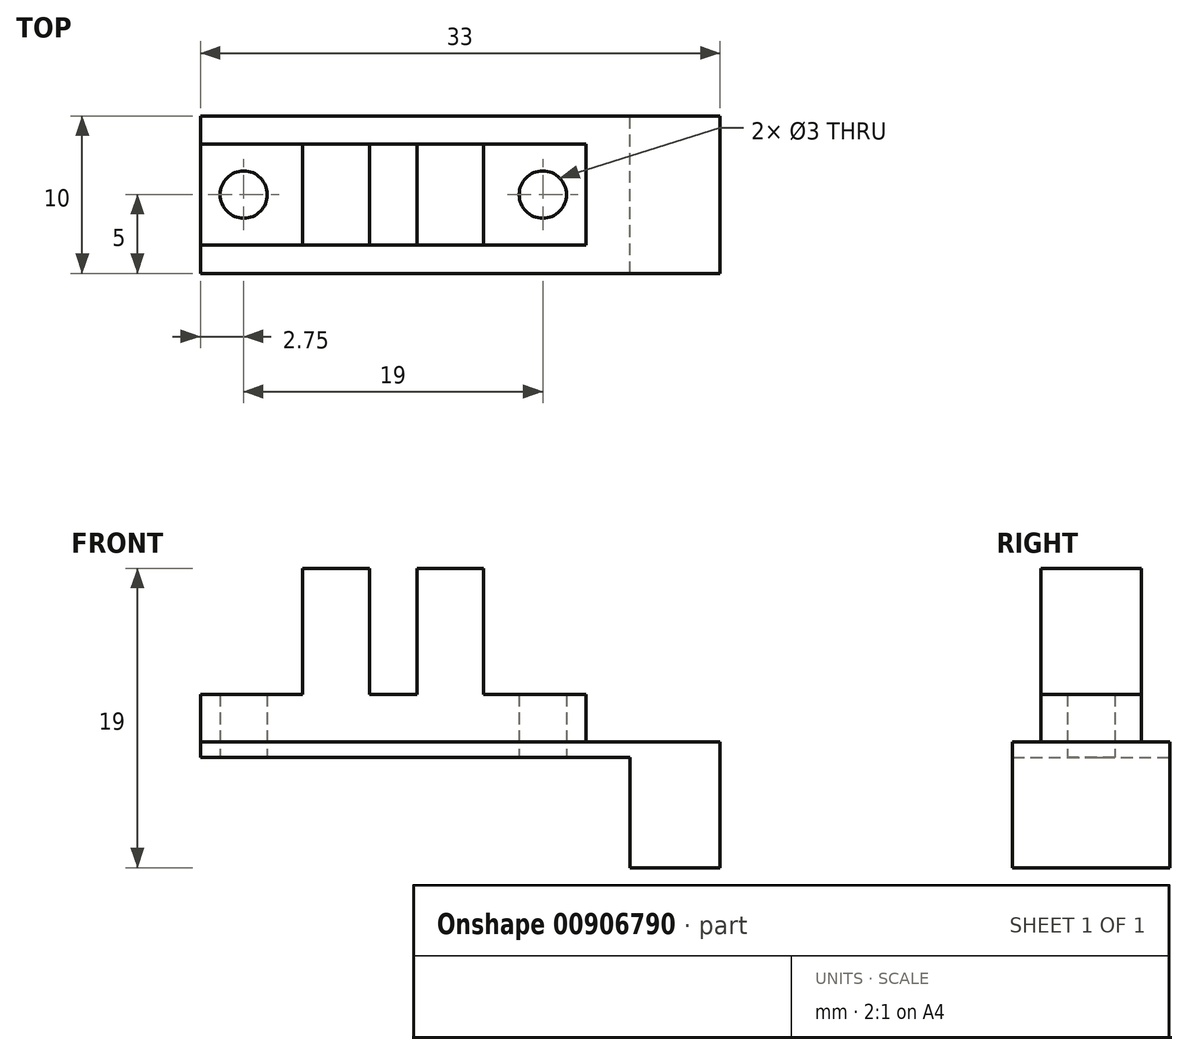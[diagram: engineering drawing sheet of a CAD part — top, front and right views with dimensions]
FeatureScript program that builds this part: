
annotation { "Feature Type Name" : "Feature", "Feature Type Description" : "" }
export const myFeature = defineFeature(function(context is Context, id is Id, definition is map)
    precondition{}
    {
        {
            var Q0;
            Q0=qCreatedBy(makeId("Top.planeOp"),FACE);
            var sketch = newSketch(context, id + "F0", { "sketchPlane" : qUnion([Q0])});
            skCircle(sketch, "E0", {"center": v(-9.5, 0) * mm, "radius": 1.5 * mm});
            skCircle(sketch, "E1", {"center": v(9.5, 0) * mm, "radius": 1.5 * mm});
            skLineSegment(sketch, "E2.bottom", {"start": v(12.25, -5) * mm, "end": v(-12.25, -5) * mm});
            skLineSegment(sketch, "E2.top", {"start": v(12.25, 5) * mm, "end": v(-12.25, 5) * mm});
            skLineSegment(sketch, "E2.left", {"start": v(12.25, -5) * mm, "end": v(12.25, 5) * mm});
            skLineSegment(sketch, "E2.right", {"start": v(-12.25, -5) * mm, "end": v(-12.25, 5) * mm});
            skPoint(sketch, "E2.middle", {"position": v(0, 0) * mm});
            skLineSegment(sketch, "E3", {"start": v(12.25, 5) * mm, "end": v(20.75, 5) * mm});
            skLineSegment(sketch, "E4", {"start": v(20.75, 5) * mm, "end": v(20.75, -5) * mm});
            skLineSegment(sketch, "E5", {"start": v(20.75, -5) * mm, "end": v(12.25, -5) * mm});
            skSolve(sketch);
        }
        {
            var Q0;
            Q0=makeQuery(id+"F0.imprint","IMPRINT",FACE,{"disambiguationData":[TD([[makeQuery(id+"F0.imprint","IMPRINT",EDGE,{"derivedFrom":sQuery(id+"F0.wireOp",EDGE,"E0")}),-1.0]])]});
            var Q1;
            Q1=makeQuery(id+"F0.imprint","IMPRINT",FACE,{"disambiguationData":[TD([[makeQuery(id+"F0.imprint","IMPRINT",EDGE,{"derivedFrom":sQuery(id+"F0.wireOp",EDGE,"E2.left")}),-1.0]])]});
            extrude(context, id + "F1", {"entities" : qUnion([Q0, Q1]), "depth" : 1 * mm, "offsetDistance" : 25 * mm});
        }
        {
            var Q0;
            Q0=makeQuery(id+"F1.opExtrude","CAP_FACE",FACE,{"disambiguationData":[OSD([sQuery(id+"F0.wireOp",EDGE,"E0"),sQuery(id+"F0.wireOp",EDGE,"E1"),sQuery(id+"F0.wireOp",EDGE,"E2.bottom"),sQuery(id+"F0.wireOp",EDGE,"E2.top"),sQuery(id+"F0.wireOp",EDGE,"E2.right"),sQuery(id+"F0.wireOp",EDGE,"E3"),sQuery(id+"F0.wireOp",EDGE,"E4"),sQuery(id+"F0.wireOp",EDGE,"E5")])],"isStart":false});
            var sketch = newSketch(context, id + "F2", { "sketchPlane" : qUnion([Q0])});
            skLineSegment(sketch, "E6.bottom", {"start": v(-12.25, -3.2) * mm, "end": v(12.25, -3.2) * mm});
            skLineSegment(sketch, "E6.top", {"start": v(-12.25, 3.2) * mm, "end": v(12.25, 3.2) * mm});
            skLineSegment(sketch, "E6.left", {"start": v(-12.25, -3.2) * mm, "end": v(-12.25, 3.2) * mm});
            skLineSegment(sketch, "E6.right", {"start": v(12.25, -3.2) * mm, "end": v(12.25, 3.2) * mm});
            skPoint(sketch, "E6.middle", {"position": v(0, 0) * mm});
            skLineSegment(sketch, "E7", {"start": v(-5.75, 3.2) * mm, "end": v(-5.75, -3.2) * mm});
            skLineSegment(sketch, "E8", {"start": v(-1.5, 3.2) * mm, "end": v(-1.5, -3.2) * mm});
            skLineSegment(sketch, "E9", {"start": v(1.5, -3.2) * mm, "end": v(1.5, 3.2) * mm});
            skLineSegment(sketch, "E10", {"start": v(5.75, 3.2) * mm, "end": v(5.75, -3.2) * mm});
            skLineSegment(sketch, "E11", {"start": v(0, 3.2) * mm, "end": v(0, -3.2) * mm, "construction": true});
            skSolve(sketch);
        }
        {
            var Q0;
            {var subQ1=sQuery(id+"F2.wireOp",EDGE,"E6.left");Q0=makeQuery(id+"F2.imprint","IMPRINT",FACE,{"disambiguationData":[TD([[makeQuery(id+"F2.imprint","IMPRINT",EDGE,{"derivedFrom":subQ1}),-1.0]])]});}
            var Q1;
            {var subQ0=sQuery(id+"F2.wireOp",EDGE,"E8");Q1=makeQuery(id+"F2.imprint","IMPRINT",FACE,{"disambiguationData":[TD([[makeQuery(id+"F2.imprint","IMPRINT",EDGE,{"derivedFrom":subQ0}),1.0]])]});}
            var Q2;
            {var subQ1=sQuery(id+"F2.wireOp",EDGE,"E6.right");Q2=makeQuery(id+"F2.imprint","IMPRINT",FACE,{"disambiguationData":[TD([[makeQuery(id+"F2.imprint","IMPRINT",EDGE,{"derivedFrom":subQ1}),1.0]])]});}
            extrude(context, id + "F3", {"entities" : qUnion([Q0, Q1, Q2]), "operationType" : NewBodyOperationType.ADD, "depth" : 3 * mm, "offsetDistance" : 25 * mm});
        }
        {
            var Q0;
            {var subQ0=sQuery(id+"F2.wireOp",EDGE,"E7");Q0=makeQuery(id+"F2.imprint","IMPRINT",FACE,{"disambiguationData":[TD([[makeQuery(id+"F2.imprint","IMPRINT",EDGE,{"derivedFrom":subQ0}),1.0]])]});}
            var Q1;
            {var subQ0=sQuery(id+"F2.wireOp",EDGE,"E9");Q1=makeQuery(id+"F2.imprint","IMPRINT",FACE,{"disambiguationData":[TD([[makeQuery(id+"F2.imprint","IMPRINT",EDGE,{"derivedFrom":subQ0}),-1.0]])]});}
            extrude(context, id + "F4", {"entities" : qUnion([Q0, Q1]), "operationType" : NewBodyOperationType.ADD, "depth" : 11 * mm, "offsetDistance" : 25 * mm});
        }
        {
            var Q0;
            Q0=makeQuery(id+"F1.opExtrude","CAP_FACE",FACE,{"disambiguationData":[OSD([sQuery(id+"F0.wireOp",EDGE,"E0"),sQuery(id+"F0.wireOp",EDGE,"E1"),sQuery(id+"F0.wireOp",EDGE,"E2.bottom"),sQuery(id+"F0.wireOp",EDGE,"E2.top"),sQuery(id+"F0.wireOp",EDGE,"E2.right"),sQuery(id+"F0.wireOp",EDGE,"E3"),sQuery(id+"F0.wireOp",EDGE,"E4"),sQuery(id+"F0.wireOp",EDGE,"E5")])],"isStart":true});
            var sketch = newSketch(context, id + "F5", { "sketchPlane" : qUnion([Q0])});
            skLineSegment(sketch, "E12.bottom", {"start": v(20.75, 5) * mm, "end": v(15.05, 5) * mm});
            skLineSegment(sketch, "E12.top", {"start": v(20.75, -5) * mm, "end": v(15.05, -5) * mm});
            skLineSegment(sketch, "E12.left", {"start": v(20.75, 5) * mm, "end": v(20.75, -5) * mm});
            skLineSegment(sketch, "E12.right", {"start": v(15.05, 5) * mm, "end": v(15.05, -5) * mm});
            skSolve(sketch);
        }
        {
            var Q0;
            Q0=makeQuery(id+"F5.imprint","IMPRINT",FACE,{"disambiguationData":[TD([[makeQuery(id+"F5.imprint","IMPRINT",EDGE,{"derivedFrom":sQuery(id+"F5.wireOp",EDGE,"E12.bottom")}),1.0]])]});
            extrude(context, id + "F6", {"entities" : qUnion([Q0]), "operationType" : NewBodyOperationType.ADD, "depth" : 7 * mm, "offsetDistance" : 25 * mm});
        }
    });
